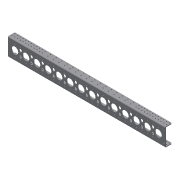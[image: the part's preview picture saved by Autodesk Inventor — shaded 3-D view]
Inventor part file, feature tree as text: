
AUTODESK INVENTOR PART (.ipt)
format: ipt  version: 2013 (Build 170138000, 138)  size: 351,232 bytes
history: native  units: in
note: dims shown in document units (in); Inventor stores cm internally (conversion verified against a paired STEP export)
features: chamfer x1, other x1, imported_body x1
ambient origin geometry x8: Origin, YZ Plane, XZ Plane, XY Plane, X Axis, Y Axis, Z Axis, Center Point
feature tree (3):
  chamfer  "Chamfer1"  [1 undecoded]
  other  "217-3648-002 Rev11"
  imported_body  "Base1"
note: 1 required parameter value undecoded (feature->parameter linkage not recoverable at this tier; creation-order binding heuristic only, values carry confidence <= 0.55)
